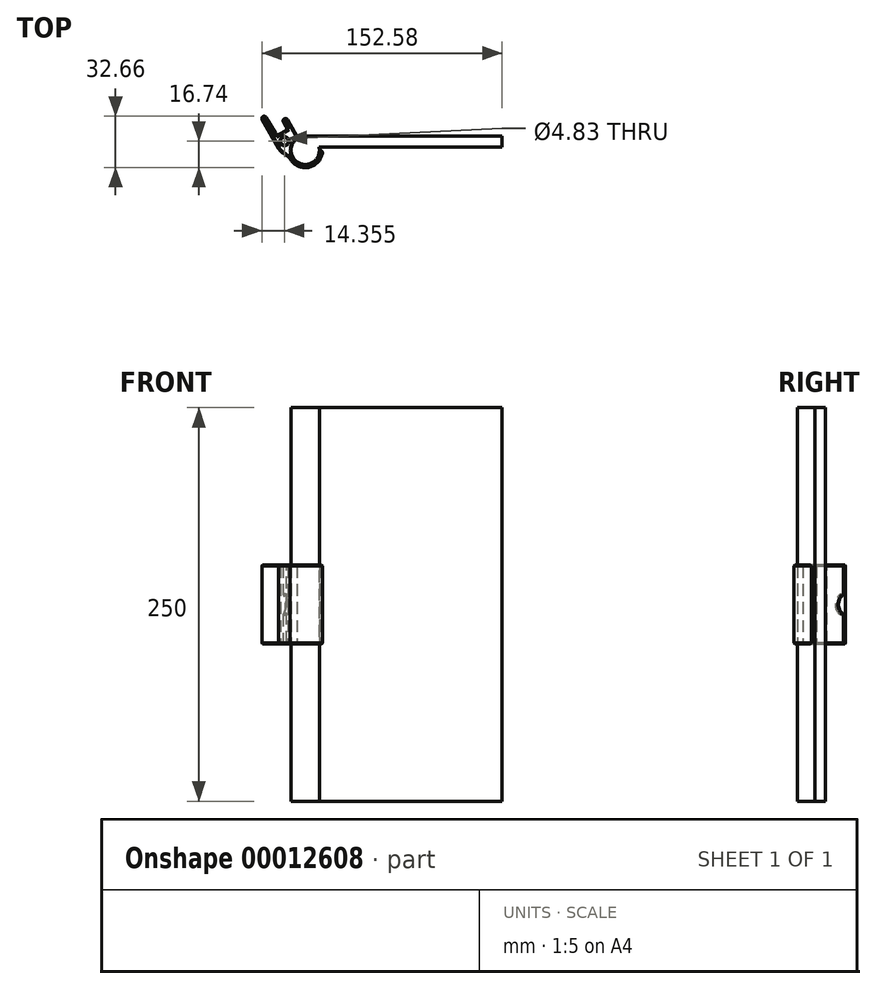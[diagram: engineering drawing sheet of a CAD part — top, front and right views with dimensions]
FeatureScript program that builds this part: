
annotation { "Feature Type Name" : "Feature", "Feature Type Description" : "" }
export const myFeature = defineFeature(function(context is Context, id is Id, definition is map)
    precondition{}
    {
        {
            var Q0;
            Q0=qCreatedBy(makeId("Top.planeOp"),FACE);
            var sketch = newSketch(context, id + "F0", { "sketchPlane" : qUnion([Q0])});
            skArc(sketch, "E0", {"start": v(9, 0) * mm, "mid": v(-4.5, -7.8) * mm, "end": v(-4.5, 7.8) * mm});
            skLineSegment(sketch, "E1", {"start": v(0, 0) * mm, "end": v(22.7, 0) * mm, "construction": true});
            skLineSegment(sketch, "E2", {"start": v(0, 0) * mm, "end": v(-19.43, 33.65) * mm, "construction": true});
            skLineSegment(sketch, "E3", {"start": v(9, 0) * mm, "end": v(11, 0) * mm});
            skLineSegment(sketch, "E4", {"start": v(-16.85, 1.18) * mm, "end": v(-28.12, 20.71) * mm});
            skLineSegment(sketch, "E5", {"start": v(-28.12, 20.71) * mm, "end": v(-25.53, 22.21) * mm});
            skLineSegment(sketch, "E6", {"start": v(-25.53, 22.21) * mm, "end": v(-18.03, 9.22) * mm});
            skLineSegment(sketch, "E7", {"start": v(-18.03, 9.22) * mm, "end": v(-11.1, 13.22) * mm});
            skLineSegment(sketch, "E8", {"start": v(-11.1, 13.22) * mm, "end": v(-14.6, 19.28) * mm});
            skLineSegment(sketch, "E9", {"start": v(-14.6, 19.28) * mm, "end": v(-12, 20.78) * mm});
            skLineSegment(sketch, "E10", {"start": v(40.86, 23.59) * mm, "end": v(-39.8, -22.98) * mm, "construction": true});
            skLineSegment(sketch, "E11", {"start": v(-12, 20.78) * mm, "end": v(-4.5, 7.8) * mm});
            skCircle(sketch, "E12", {"center": v(-13.22, 5.74) * mm, "radius": 2.42 * mm});
            skArc(sketch, "E13", {"start": v(11, 0) * mm, "mid": v(2.85, -10.63) * mm, "end": v(-9.53, -5.5) * mm});
            skFitSpline(sketch, "E14", {"points": [v(-16.85, 1.18) * mm, v(-9.53, -5.5) * mm], "startDerivative": vector(3.28, -8.37) * mm, "endDerivative": vector(4.57, -7.4) * mm});
            skSolve(sketch);
        }
        {
            var Q0;
            Q0=qSketchRegion(id+"F0",true);
            extrude(context, id + "F1", {"entities" : qUnion([Q0]), "depth" : 50 * mm, "symmetric" : true});
        }
        {
            var Q0;
            Q0=makeQuery(id+"F1.opExtrude","SWEPT_EDGE",EDGE,{"disambiguationData":[OSD([sQuery(id+"F0.wireOp",EDGE,"E5"),sQuery(id+"F0.wireOp",EDGE,"E6")])]});
            var Q1;
            Q1=makeQuery(id+"F1.opExtrude","SWEPT_EDGE",EDGE,{"disambiguationData":[OSD([sQuery(id+"F0.wireOp",EDGE,"E4"),sQuery(id+"F0.wireOp",EDGE,"E5")])]});
            var Q2;
            Q2=makeQuery(id+"F1.opExtrude","SWEPT_EDGE",EDGE,{"disambiguationData":[OSD([sQuery(id+"F0.wireOp",EDGE,"E8"),sQuery(id+"F0.wireOp",EDGE,"E9")])]});
            var Q3;
            Q3=makeQuery(id+"F1.opExtrude","SWEPT_EDGE",EDGE,{"disambiguationData":[OSD([sQuery(id+"F0.wireOp",EDGE,"E9"),sQuery(id+"F0.wireOp",EDGE,"E11")])]});
            var Q4;
            Q4=makeQuery(id+"F1.opExtrude","SWEPT_EDGE",EDGE,{"disambiguationData":[OSD([sQuery(id+"F0.wireOp",EDGE,"E0"),sQuery(id+"F0.wireOp",EDGE,"E3")])]});
            var Q5;
            Q5=makeQuery(id+"F1.opExtrude","SWEPT_EDGE",EDGE,{"disambiguationData":[OSD([sQuery(id+"F0.wireOp",EDGE,"E3"),sQuery(id+"F0.wireOp",EDGE,"4a55d94b-3234-4131-b911-7e764871b69e")])]});
            fillet(context, id + "F2", {"entities" : qUnion([Q0, Q1, Q2, Q3, Q4, Q5]), "radius" : 1.5 * mm, "tangentPropagation" : true, "allowEdgeOverflow" : false});
        }
        {
            var Q0;
            Q0=makeQuery(id+"F1.opExtrude","SWEPT_EDGE",EDGE,{"disambiguationData":[OSD([sQuery(id+"F0.wireOp",EDGE,"E0"),sQuery(id+"F0.wireOp",EDGE,"E11")])]});
            fillet(context, id + "F3", {"entities" : qUnion([Q0]), "radius" : 2 * mm, "tangentPropagation" : true, "allowEdgeOverflow" : false});
        }
        {
            var Q0;
            Q0=makeQuery(id+"F1.opExtrude","SWEPT_FACE",FACE,{"disambiguationData":[OSD([sQuery(id+"F0.wireOp",EDGE,"E11")])]});
            var sketch = newSketch(context, id + "F4", { "sketchPlane" : qUnion([Q0])});
            skCircle(sketch, "E15", {"center": v(27.5, 0) * mm, "radius": 7 * mm});
            skPoint(sketch, "E16", {"position": v(10.82, 0) * mm});
            skPoint(sketch, "E17", {"position": v(22.5, 0) * mm});
            skSolve(sketch);
        }
        {
            var Q0;
            Q0=qSketchRegion(id+"F4",true);
            var Q1;
            Q1=makeQuery(id+"F1.opExtrude","SWEPT_FACE",FACE,{"disambiguationData":[OSD([sQuery(id+"F0.wireOp",EDGE,"E8")])]});
            extrude(context, id + "F5", {"entities" : qUnion([Q0]), "operationType" : NewBodyOperationType.REMOVE, "endBound" : BoundingType.UP_TO_SURFACE, "oppositeDirection" : true, "endBoundEntityFace" : qUnion([Q1]), "depth" : 25 * mm});
        }
        {
            var Q0;
            Q0=makeQuery(id+"F1.opExtrude","CAP_FACE",FACE,{"disambiguationData":[OSD([sQuery(id+"F0.wireOp",EDGE,"E0"),sQuery(id+"F0.wireOp",EDGE,"E3"),sQuery(id+"F0.wireOp",EDGE,"E4"),sQuery(id+"F0.wireOp",EDGE,"E5"),sQuery(id+"F0.wireOp",EDGE,"E6"),sQuery(id+"F0.wireOp",EDGE,"E7"),sQuery(id+"F0.wireOp",EDGE,"E8"),sQuery(id+"F0.wireOp",EDGE,"E9"),sQuery(id+"F0.wireOp",EDGE,"4a55d94b-3234-4131-b911-7e764871b69e"),sQuery(id+"F0.wireOp",EDGE,"E11")])],"isStart":false});
            var Q1;
            Q1=makeQuery(id+"F1.opExtrude","CAP_FACE",FACE,{"disambiguationData":[OSD([sQuery(id+"F0.wireOp",EDGE,"E0"),sQuery(id+"F0.wireOp",EDGE,"E3"),sQuery(id+"F0.wireOp",EDGE,"E4"),sQuery(id+"F0.wireOp",EDGE,"E5"),sQuery(id+"F0.wireOp",EDGE,"E6"),sQuery(id+"F0.wireOp",EDGE,"E7"),sQuery(id+"F0.wireOp",EDGE,"E8"),sQuery(id+"F0.wireOp",EDGE,"E9"),sQuery(id+"F0.wireOp",EDGE,"4a55d94b-3234-4131-b911-7e764871b69e"),sQuery(id+"F0.wireOp",EDGE,"E11")])],"isStart":true});
            chamfer(context, id + "F6", {"entities" : qUnion([Q0, Q1]), "width" : .5 * mm, "tangentPropagation" : true});
        }
        {
            var Q0;
            Q0=makeQuery(id+"F1.opExtrude","SWEPT_EDGE",EDGE,{"disambiguationData":[OSD([sQuery(id+"F0.wireOp",EDGE,"E6"),sQuery(id+"F0.wireOp",EDGE,"E7")])]});
            var Q1;
            Q1=makeQuery(id+"F1.opExtrude","SWEPT_EDGE",EDGE,{"disambiguationData":[OSD([sQuery(id+"F0.wireOp",EDGE,"E7"),sQuery(id+"F0.wireOp",EDGE,"E8")])]});
            fillet(context, id + "F7", {"entities" : qUnion([Q0, Q1]), "radius" : 2 * mm, "tangentPropagation" : true, "allowEdgeOverflow" : false});
        }
        {
            var Q0;
            Q0=qCreatedBy(makeId("Top.planeOp"),FACE);
            var sketch = newSketch(context, id + "F8", { "sketchPlane" : qUnion([Q0])});
            skCircle(sketch, "E18", {"center": v(0, 0) * mm, "radius": 9 * mm});
            skLineSegment(sketch, "E19.bottom", {"start": v(0, 9) * mm, "end": v(125, 9) * mm});
            skLineSegment(sketch, "E19.top", {"start": v(0, 2.14) * mm, "end": v(125, 2.14) * mm});
            skLineSegment(sketch, "E19.left", {"start": v(0, 9) * mm, "end": v(0, 2.14) * mm});
            skLineSegment(sketch, "E19.right", {"start": v(125, 9) * mm, "end": v(125, 2.14) * mm});
            skLineSegment(sketch, "E20", {"start": v(-32.62, 38.23) * mm, "end": v(28.74, -33.68) * mm, "construction": true});
            skSolve(sketch);
        }
        {
            var Q0;
            Q0=qSketchRegion(id+"F8",true);
            extrude(context, id + "F9", {"entities" : qUnion([Q0]), "depth" : 250 * mm, "symmetric" : true});
        }
        {
            var Q0;
            Q0=makeQuery(id+"F5.boolean.opBoolean","COPY",FACE,{"derivedFrom":makeQuery(id+"F5.opExtrude","SWEPT_FACE",FACE,{"disambiguationData":[OSD([sQuery(id+"F4.wireOp",EDGE,"E15")])]})});
            chamfer(context, id + "F10", {"entities" : qUnion([Q0]), "width" : 1 * mm, "tangentPropagation" : true});
        }
    });
